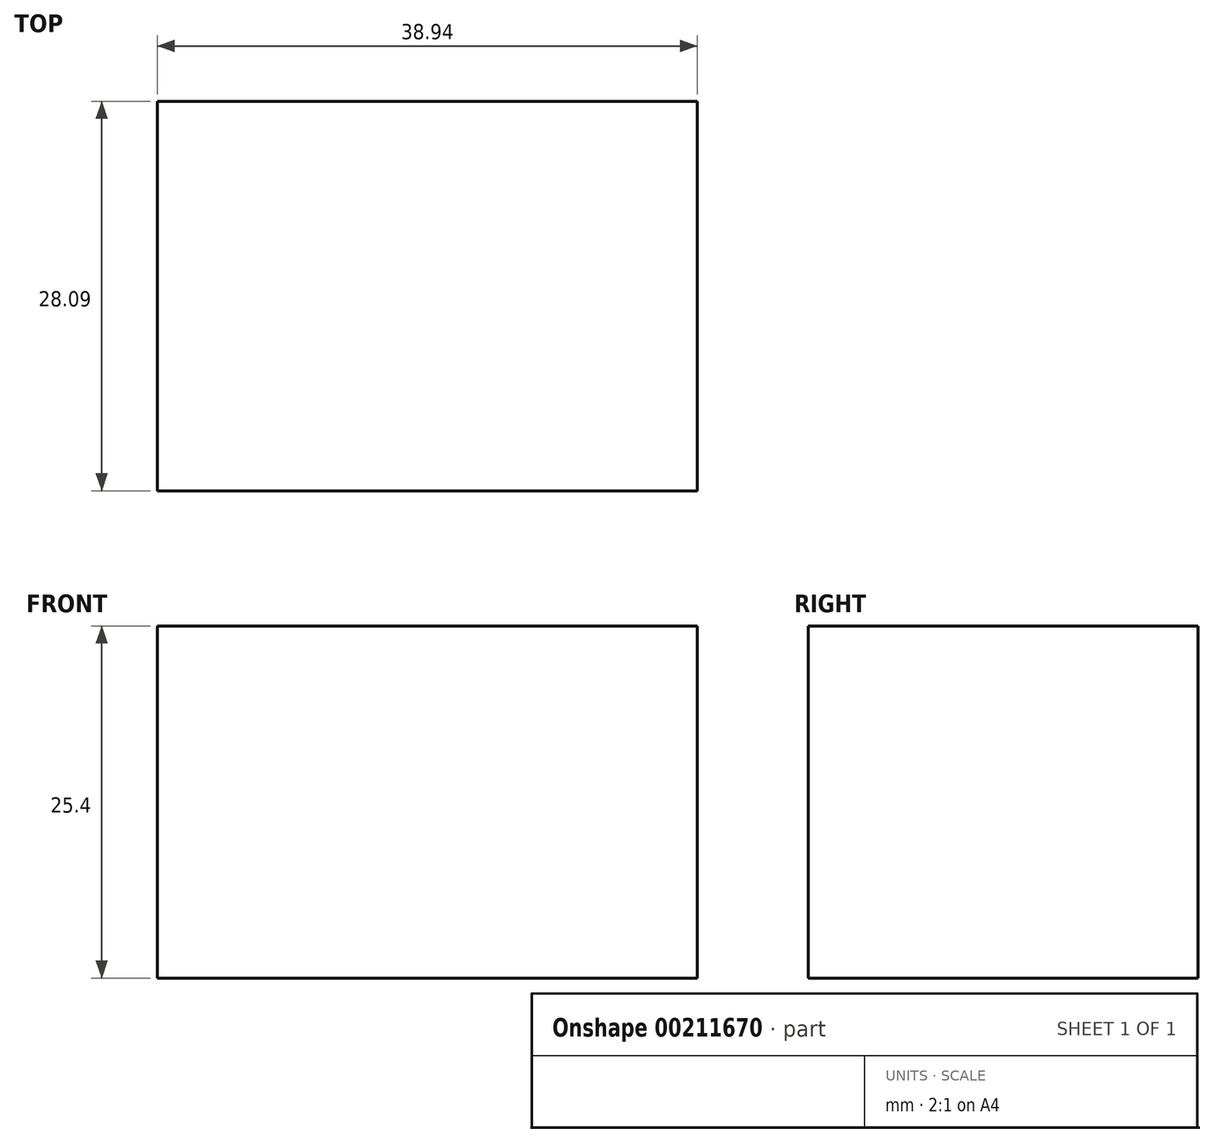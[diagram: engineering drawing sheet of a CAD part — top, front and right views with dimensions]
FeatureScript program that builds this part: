
annotation { "Feature Type Name" : "Feature", "Feature Type Description" : "" }
export const myFeature = defineFeature(function(context is Context, id is Id, definition is map)
    precondition{}
    {
        {
            var Q0;
            Q0=qCreatedBy(makeId("Top.planeOp"),FACE);
            var sketch = newSketch(context, id + "F0", { "sketchPlane" : qUnion([Q0])});
            skLineSegment(sketch, "E0.bottom", {"start": v(0, 0) * mm, "end": v(38.94, 0) * mm});
            skLineSegment(sketch, "E0.top", {"start": v(0, 28.1) * mm, "end": v(38.94, 28.1) * mm});
            skLineSegment(sketch, "E0.left", {"start": v(0, 0) * mm, "end": v(0, 28.1) * mm});
            skLineSegment(sketch, "E0.right", {"start": v(38.94, 0) * mm, "end": v(38.94, 28.1) * mm});
            skSolve(sketch);
        }
        {
            var Q0;
            Q0 = qConstructionFilter(qBodyType(qCreatedBy(id + "F0" ,EDGE), BodyType.WIRE), ConstructionObject.NO);
            extrude(context, id + "F1", {"bodyType" : ToolBodyType.SURFACE, "surfaceEntities" : qUnion([Q0]), "depth" : 25.4 * mm});
        }
    });
